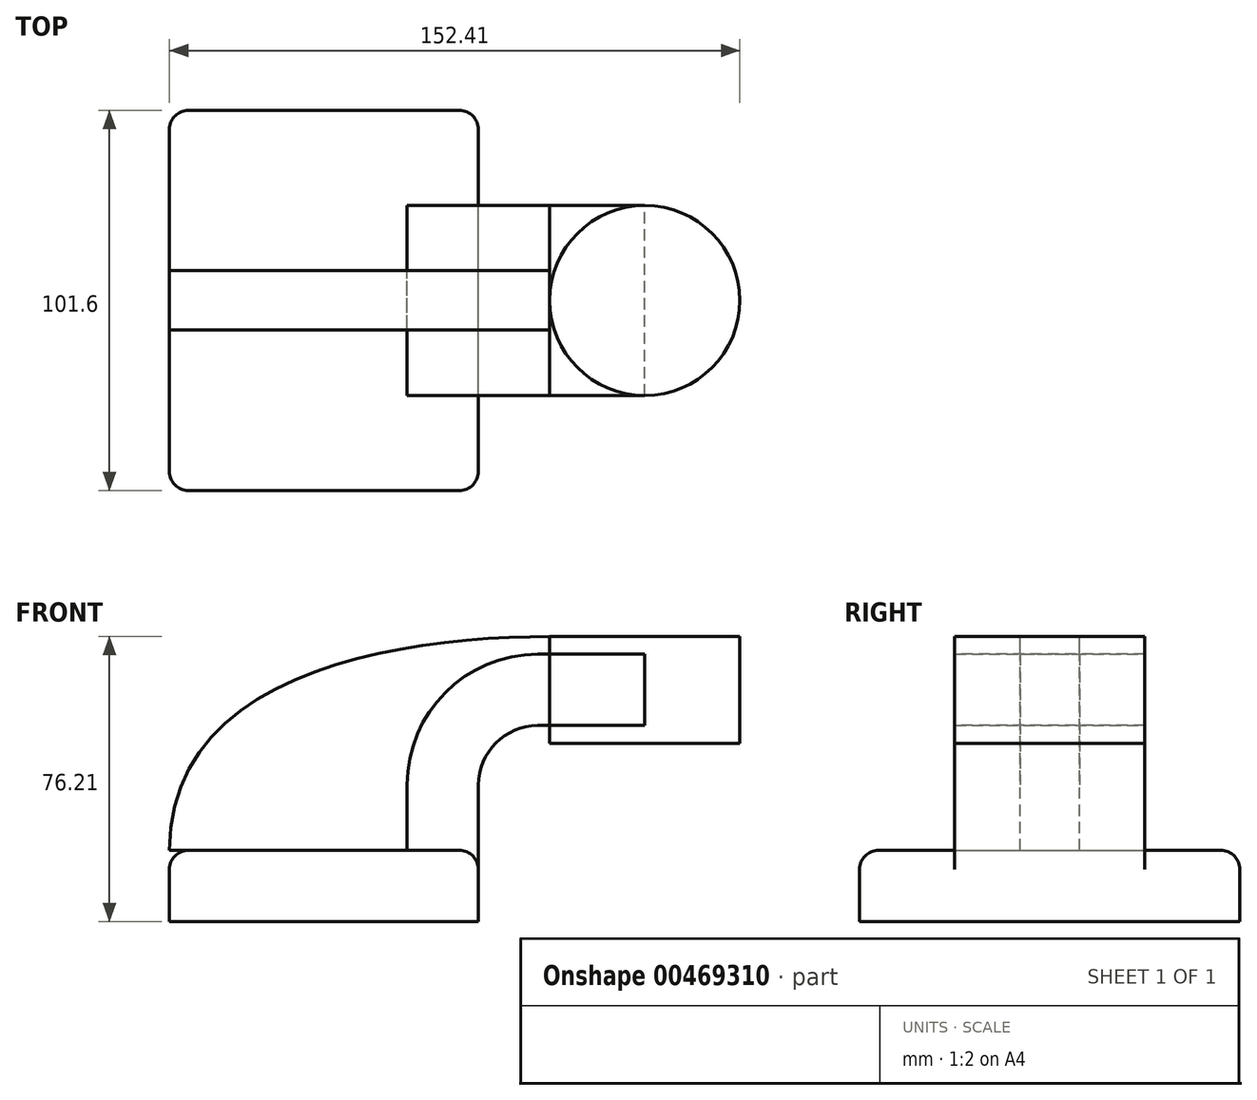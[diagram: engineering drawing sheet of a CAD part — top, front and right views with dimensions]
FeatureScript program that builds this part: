
annotation { "Feature Type Name" : "Feature", "Feature Type Description" : "" }
export const myFeature = defineFeature(function(context is Context, id is Id, definition is map)
    precondition{}
    {
        {
            var Q0;
            Q0=qCreatedBy(makeId("Front.planeOp"),FACE);
            var sketch = newSketch(context, id + "F0", { "sketchPlane" : qUnion([Q0])});
            skLineSegment(sketch, "E0.bottom", {"start": v(41.28, -9.52) * mm, "end": v(-41.27, -9.52) * mm});
            skLineSegment(sketch, "E0.top", {"start": v(41.27, 9.53) * mm, "end": v(-41.28, 9.53) * mm});
            skLineSegment(sketch, "E0.left", {"start": v(41.28, -9.52) * mm, "end": v(41.28, 9.53) * mm});
            skLineSegment(sketch, "E0.right", {"start": v(-41.27, -9.52) * mm, "end": v(-41.28, 9.53) * mm});
            skPoint(sketch, "E0.middle", {"position": v(0, 0) * mm});
            skLineSegment(sketch, "E1.bottom", {"start": v(111.13, 38.1) * mm, "end": v(60.32, 38.1) * mm});
            skLineSegment(sketch, "E1.top", {"start": v(111.13, 66.68) * mm, "end": v(60.33, 66.67) * mm});
            skLineSegment(sketch, "E1.left", {"start": v(111.13, 38.1) * mm, "end": v(111.13, 66.67) * mm});
            skLineSegment(sketch, "E1.right", {"start": v(60.33, 38.1) * mm, "end": v(60.33, 66.68) * mm});
            skPoint(sketch, "E1.middle", {"position": v(85.73, 52.39) * mm});
            skLineSegment(sketch, "E2", {"start": v(41.27, 9.53) * mm, "end": v(41.27, 27) * mm});
            skArc(sketch, "E3", {"start": v(41.27, 27) * mm, "mid": v(45.92, 38.23) * mm, "end": v(57.15, 42.88) * mm});
            skLineSegment(sketch, "E4", {"start": v(57.15, 42.88) * mm, "end": v(85.73, 42.88) * mm});
            skLineSegment(sketch, "E5.0", {"start": v(57.15, 61.93) * mm, "end": v(85.72, 61.93) * mm});
            skArc(sketch, "E5.1", {"start": v(22.22, 27) * mm, "mid": v(32.45, 51.7) * mm, "end": v(57.15, 61.93) * mm});
            skLineSegment(sketch, "E5.2", {"start": v(22.22, 9.53) * mm, "end": v(22.22, 27) * mm});
            skFitSpline(sketch, "E6", {"points": [v(-41.28, 9.53) * mm, v(60.32, 66.67) * mm], "startDerivative": vector(0.1, 144.56) * mm, "endDerivative": vector(118.64, 0.3) * mm});
            skLineSegment(sketch, "E7", {"start": v(85.72, 42.88) * mm, "end": v(85.72, 61.93) * mm});
            skLineSegment(sketch, "E8", {"start": v(85.73, 61.93) * mm, "end": v(85.72, 66.68) * mm});
            skLineSegment(sketch, "E9", {"start": v(85.73, 66.68) * mm, "end": v(85.73, 38.1) * mm});
            skSolve(sketch);
        }
        {
            var Q0;
            Q0=makeQuery(id+"F0.imprint","IMPRINT",FACE,{"disambiguationData":[TD([[makeQuery(id+"F0.imprint","IMPRINT",EDGE,{"derivedFrom":sQuery(id+"F0.wireOp",EDGE,"E0.bottom")}),-1.0]])]});
            extrude(context, id + "F1", {"entities" : qUnion([Q0]), "endBound" : BoundingType.SYMMETRIC, "depth" : 101.6 * mm});
        }
        {
            var Q0;
            {var subQ1=sQuery(id+"F0.wireOp",EDGE,"E2");Q0=makeQuery(id+"F0.imprint","IMPRINT",FACE,{"disambiguationData":[TD([[makeQuery(id+"F0.imprint","IMPRINT",EDGE,{"derivedFrom":subQ1}),1.0]])]});}
            var Q1;
            {var subQ5=sQuery(id+"F0.wireOp",EDGE,"E7");Q1=makeQuery(id+"F0.imprint","IMPRINT",FACE,{"disambiguationData":[TD([[makeQuery(id+"F0.imprint","IMPRINT",EDGE,{"derivedFrom":subQ5}),1.0]])]});}
            extrude(context, id + "F2", {"entities" : qUnion([Q0, Q1]), "operationType" : NewBodyOperationType.ADD, "endBound" : BoundingType.SYMMETRIC, "depth" : 50.8 * mm});
        }
        {
            var Q0;
            {var subQ0=sQuery(id+"F0.wireOp",EDGE,"E5.1");Q0=makeQuery(id+"F0.imprint","IMPRINT",FACE,{"disambiguationData":[TD([[makeQuery(id+"F0.imprint","IMPRINT",EDGE,{"derivedFrom":subQ0}),1.0]])]});}
            extrude(context, id + "F3", {"entities" : qUnion([Q0]), "operationType" : NewBodyOperationType.ADD, "endBound" : BoundingType.SYMMETRIC, "depth" : 15.88 * mm});
        }
        {
            var Q0;
            {var subQ0=sQuery(id+"F0.wireOp",EDGE,"E1.left");Q0=makeQuery(id+"F0.imprint","IMPRINT",FACE,{"disambiguationData":[TD([[makeQuery(id+"F0.imprint","IMPRINT",EDGE,{"derivedFrom":subQ0}),1.0]])]});}
            var Q1;
            Q1=sQuery(id+"F0.wireOp",EDGE,"E9");
            revolve(context, id + "F4", {"operationType" : NewBodyOperationType.ADD, "entities" : qUnion([Q0]), "axis" : qUnion([Q1]), "revolveType" : RevolveType.FULL});
        }
        {
            var Q0;
            {var subQ0=sQuery(id+"F0.wireOp",EDGE,"E4");var subQ1=sQuery(id+"F0.wireOp",EDGE,"E1.right");var subQ2=makeQuery(id+"F0.imprint","INTERSECT",VERTEX,{"derivedFrom":[subQ1,subQ0]});Q0=makeQuery(id+"F0.imprint","IMPRINT",FACE,{"disambiguationData":[TD([[makeQuery(id+"F0.imprint","IMPRINT",EDGE,{"disambiguationData":[TD([[subQ2,-1.0]])],"derivedFrom":subQ1}),-1.0]])]});}
            extrude(context, id + "F5", {"entities" : qUnion([Q0]), "endBound" : BoundingType.SYMMETRIC, "depth" : 50.8 * mm});
        }
        {
            var Q0;
            {var subQ3=sQuery(id+"F0.wireOp",EDGE,"E9");var subQ5=sQuery(id+"F0.wireOp",EDGE,"E5.0");var subQ6=makeQuery(id+"F0.imprint","INTERSECT",VERTEX,{"derivedFrom":[subQ5,subQ3]});Q0=makeQuery(id+"F0.imprint","IMPRINT",FACE,{"disambiguationData":[TD([[makeQuery(id+"F0.imprint","IMPRINT",EDGE,{"disambiguationData":[TD([[subQ6,1.0]])],"derivedFrom":subQ5}),1.0]])]});}
            extrude(context, id + "F6", {"entities" : qUnion([Q0]), "endBound" : BoundingType.SYMMETRIC, "depth" : 15.88 * mm});
        }
        {
            var Q0;
            Q0=makeQuery(id+"F1.opExtrude","CAP_EDGE",EDGE,{"disambiguationData":[OSD([sQuery(id+"F0.wireOp",EDGE,"E0.right")])],"isStart":true});
            var Q1;
            Q1=makeQuery(id+"F1.opExtrude","CAP_EDGE",EDGE,{"disambiguationData":[OSD([sQuery(id+"F0.wireOp",EDGE,"E0.right")])],"isStart":false});
            var Q2;
            Q2=makeQuery(id+"F1.opExtrude","CAP_EDGE",EDGE,{"disambiguationData":[OSD([sQuery(id+"F0.wireOp",EDGE,"E0.left")])],"isStart":false});
            var Q3;
            Q3=makeQuery(id+"F1.opExtrude","CAP_EDGE",EDGE,{"disambiguationData":[OSD([sQuery(id+"F0.wireOp",EDGE,"E0.left")])],"isStart":true});
            var Q4;
            Q4=makeQuery(id+"F3.opExtrude","CAP_EDGE",EDGE,{"disambiguationData":[OSD([sQuery(id+"F0.wireOp",EDGE,"E6")])],"isStart":false});
            var Q5;
            Q5=makeQuery(id+"F3.opExtrude","CAP_EDGE",EDGE,{"disambiguationData":[OSD([sQuery(id+"F0.wireOp",EDGE,"E6")])],"isStart":true});
            var Q6;
            {var subQ0=sQuery(id+"F0.wireOp",EDGE,"E6");var subQ1=sQuery(id+"F0.wireOp",EDGE,"E0.top");var subQ2=sQuery(id+"F0.wireOp",EDGE,"E0.right");Q6=makeQuery(id+"F3.boolean.opBoolean","SPLIT",EDGE,{"disambiguationData":[TD([makeQuery(id+"F1.opExtrude","CAP_FACE",FACE,{"disambiguationData":[OSD([sQuery(id+"F0.wireOp",EDGE,"E0.bottom"),subQ1,sQuery(id+"F0.wireOp",EDGE,"E0.left"),subQ2])],"isStart":true})])],"derivedFrom":makeQuery(id+"F1.opExtrude","SWEPT_EDGE",EDGE,{"disambiguationData":[OSD([subQ1,subQ2,subQ0])]})});}
            var Q7;
            Q7=makeQuery(id+"F1.opExtrude","CAP_EDGE",EDGE,{"disambiguationData":[OSD([sQuery(id+"F0.wireOp",EDGE,"E0.top")])],"isStart":true});
            fillet(context, id + "F7", {"entities" : qUnion([Q0, Q1, Q2, Q3, Q4, Q5, Q6, Q7]), "radius" : 5.08 * mm, "tangentPropagation" : true, "allowEdgeOverflow" : false});
        }
        {
            var Q0;
            Q0=makeQuery(id+"F1.opExtrude","CAP_EDGE",EDGE,{"disambiguationData":[OSD([sQuery(id+"F0.wireOp",EDGE,"E0.left")])],"isStart":true});
            var Q1;
            Q1=makeQuery(id+"F1.opExtrude","CAP_EDGE",EDGE,{"disambiguationData":[OSD([sQuery(id+"F0.wireOp",EDGE,"E0.right")])],"isStart":true});
            var Q2;
            Q2=makeQuery(id+"F1.opExtrude","CAP_EDGE",EDGE,{"disambiguationData":[OSD([sQuery(id+"F0.wireOp",EDGE,"E0.right")])],"isStart":false});
            var Q3;
            Q3=makeQuery(id+"F1.opExtrude","CAP_EDGE",EDGE,{"disambiguationData":[OSD([sQuery(id+"F0.wireOp",EDGE,"E0.left")])],"isStart":false});
            var Q4;
            Q4=makeQuery(id+"F1.opExtrude","CAP_EDGE",EDGE,{"disambiguationData":[OSD([sQuery(id+"F0.wireOp",EDGE,"E0.top")])],"isStart":false});
            var Q5;
            Q5=makeQuery(id+"F1.opExtrude","CAP_EDGE",EDGE,{"disambiguationData":[OSD([sQuery(id+"F0.wireOp",EDGE,"E0.top")])],"isStart":true});
            var Q6;
            {var subQ0=sQuery(id+"F0.wireOp",EDGE,"E6");var subQ1=sQuery(id+"F0.wireOp",EDGE,"E0.top");var subQ2=sQuery(id+"F0.wireOp",EDGE,"E0.right");Q6=makeQuery(id+"F3.boolean.opBoolean","SPLIT",EDGE,{"disambiguationData":[TD([makeQuery(id+"F1.opExtrude","CAP_FACE",FACE,{"disambiguationData":[OSD([sQuery(id+"F0.wireOp",EDGE,"E0.bottom"),subQ1,sQuery(id+"F0.wireOp",EDGE,"E0.left"),subQ2])],"isStart":false})])],"derivedFrom":makeQuery(id+"F1.opExtrude","SWEPT_EDGE",EDGE,{"disambiguationData":[OSD([subQ1,subQ2,subQ0])]})});}
            var Q7;
            {var subQ0=sQuery(id+"F0.wireOp",EDGE,"E6");var subQ1=sQuery(id+"F0.wireOp",EDGE,"E0.top");var subQ2=sQuery(id+"F0.wireOp",EDGE,"E0.right");Q7=makeQuery(id+"F3.boolean.opBoolean","SPLIT",EDGE,{"disambiguationData":[TD([makeQuery(id+"F1.opExtrude","CAP_FACE",FACE,{"disambiguationData":[OSD([sQuery(id+"F0.wireOp",EDGE,"E0.bottom"),subQ1,sQuery(id+"F0.wireOp",EDGE,"E0.left"),subQ2])],"isStart":true})])],"derivedFrom":makeQuery(id+"F1.opExtrude","SWEPT_EDGE",EDGE,{"disambiguationData":[OSD([subQ1,subQ2,subQ0])]})});}
            var Q8;
            {var subQ0=sQuery(id+"F0.wireOp",EDGE,"E0.left");var subQ1=sQuery(id+"F0.wireOp",EDGE,"E2");var subQ2=sQuery(id+"F0.wireOp",EDGE,"E0.top");Q8=makeQuery(id+"F2.boolean.opBoolean","SPLIT",EDGE,{"disambiguationData":[TD([makeQuery(id+"F1.opExtrude","CAP_FACE",FACE,{"disambiguationData":[OSD([sQuery(id+"F0.wireOp",EDGE,"E0.bottom"),subQ2,subQ0,sQuery(id+"F0.wireOp",EDGE,"E0.right")])],"isStart":false})])],"derivedFrom":makeQuery(id+"F1.opExtrude","SWEPT_EDGE",EDGE,{"disambiguationData":[OSD([subQ2,subQ0,subQ1])]})});}
            var Q9;
            {var subQ0=sQuery(id+"F0.wireOp",EDGE,"E2");var subQ1=sQuery(id+"F0.wireOp",EDGE,"E0.top");var subQ2=sQuery(id+"F0.wireOp",EDGE,"E0.left");Q9=makeQuery(id+"F2.boolean.opBoolean","SPLIT",EDGE,{"disambiguationData":[TD([makeQuery(id+"F1.opExtrude","CAP_FACE",FACE,{"disambiguationData":[OSD([sQuery(id+"F0.wireOp",EDGE,"E0.bottom"),subQ1,subQ2,sQuery(id+"F0.wireOp",EDGE,"E0.right")])],"isStart":true})])],"derivedFrom":makeQuery(id+"F1.opExtrude","SWEPT_EDGE",EDGE,{"disambiguationData":[OSD([subQ1,subQ2,subQ0])]})});}
            fillet(context, id + "F8", {"entities" : qUnion([Q0, Q1, Q2, Q3, Q4, Q5, Q6, Q7, Q8, Q9]), "radius" : 5.08 * mm, "tangentPropagation" : true, "allowEdgeOverflow" : false});
        }
    });
